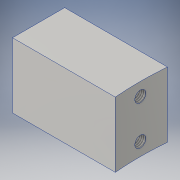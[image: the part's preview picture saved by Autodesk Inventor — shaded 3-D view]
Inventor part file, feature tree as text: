
AUTODESK INVENTOR PART (.ipt)
format: ipt  version: 2016 SP1 (Build 200210100, 210)  size: 123,904 bytes
history: native  units: in
note: dims shown in document units (in); Inventor stores cm internally (conversion verified against a paired STEP export)
features: sketch x4, extrude x2, hole x2
ambient origin geometry x8: Origin, YZ Plane, XZ Plane, XY Plane, X Axis, Y Axis, Z Axis, Center Point
bodies: Solid1 (feature_tree)
feature tree (8):
  extrude  "Extrusion1"  Depth=1.0in
  hole  "Hole1"  [1 undecoded]
  extrude  "Extrusion2"  Depth=5.75in
  hole  "Hole2"  [1 undecoded]
  sketch  "Sketch1"  dims[d0=1.0in d1=2.0in]
  sketch  "Sketch3"  dims[d2=1.25in d3=0.0in d6=0.25in]
  sketch  "Sketch4"  dims[d7=0.75in]
  sketch  "Sketch6"  dims[d8=0.211in d9=0.5in d10=0.375in d11=0.25in d12=0.5635in d13=0.679in d14=0.8108in d15=5.75in d16=11.6in d17=2.0in d18=0.0in d21=0.5in d22=0.25in d23=0.75in d24=0.211in d25=0.5in d26=0.375in d27=0.25in d28=0.5635in d29=0.679in d30=0.8108in]
note: 2 required parameter values undecoded (feature->parameter linkage not recoverable at this tier; creation-order binding heuristic only, values carry confidence <= 0.55)
